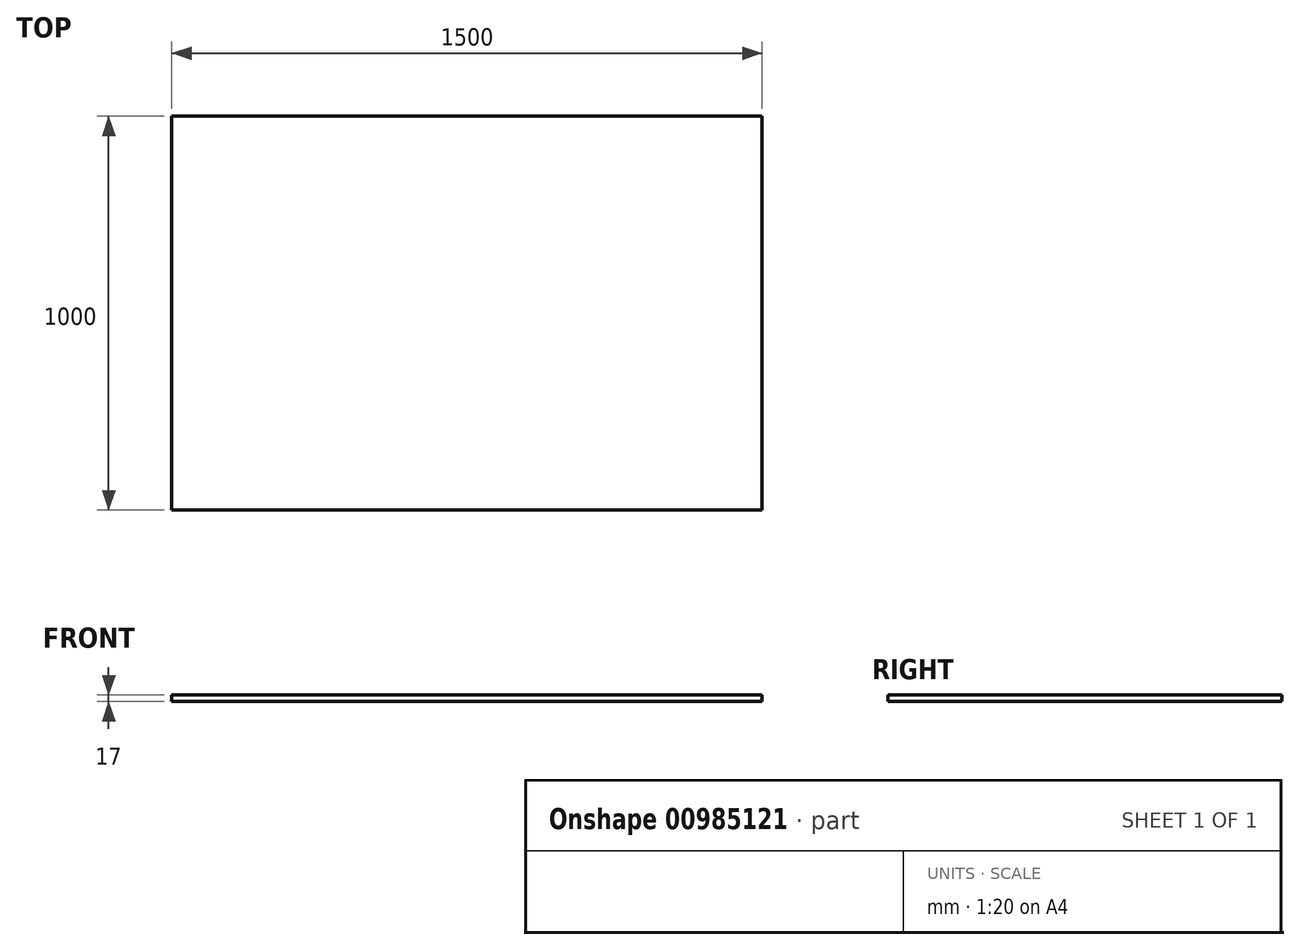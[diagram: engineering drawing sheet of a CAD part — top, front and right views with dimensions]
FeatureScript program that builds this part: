
annotation { "Feature Type Name" : "Feature", "Feature Type Description" : "" }
export const myFeature = defineFeature(function(context is Context, id is Id, definition is map)
    precondition{}
    {
        {
            var Q0;
            Q0=qCreatedBy(makeId("Top.planeOp"),FACE);
            var sketch = newSketch(context, id + "F0", { "sketchPlane" : qUnion([Q0])});
            skLineSegment(sketch, "E0.bottom", {"start": v(-747.59, 717.7) * mm, "end": v(752.41, 717.7) * mm});
            skLineSegment(sketch, "E0.top", {"start": v(-747.59, -282.3) * mm, "end": v(752.41, -282.3) * mm});
            skLineSegment(sketch, "E0.left", {"start": v(-747.59, 717.7) * mm, "end": v(-747.59, -282.3) * mm});
            skLineSegment(sketch, "E0.right", {"start": v(752.41, 717.7) * mm, "end": v(752.41, -282.3) * mm});
            skSolve(sketch);
        }
        {
            var Q0;
            Q0 = qSketchRegion(id + "F0", true);
            extrude(context, id + "F1", {"entities" : qUnion([Q0]), "depth" : 17 * mm, "offsetDistance" : 25 * mm});
        }
    });
